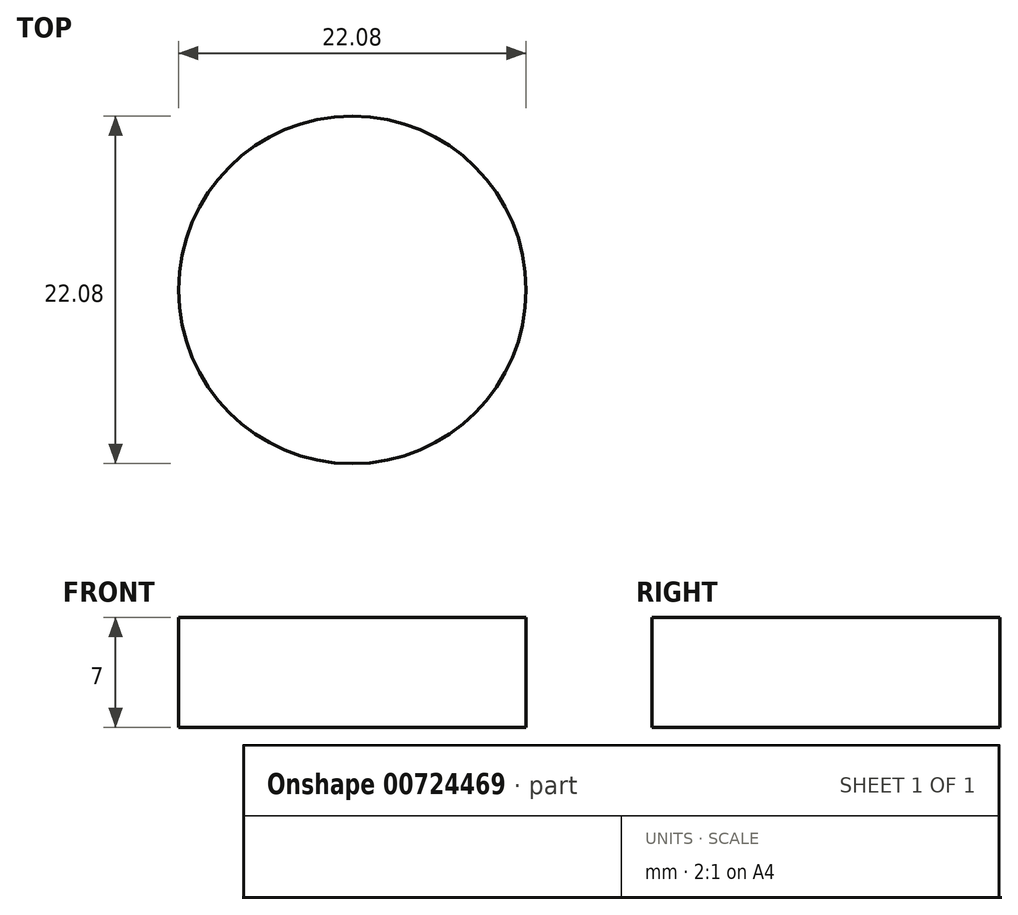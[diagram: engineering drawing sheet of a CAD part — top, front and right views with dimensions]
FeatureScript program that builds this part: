
annotation { "Feature Type Name" : "Feature", "Feature Type Description" : "" }
export const myFeature = defineFeature(function(context is Context, id is Id, definition is map)
    precondition{}
    {
        {
            var Q0;
            Q0=qCreatedBy(makeId("Top.planeOp"),FACE);
            var sketch = newSketch(context, id + "F0", { "sketchPlane" : qUnion([Q0])});
            skCircle(sketch, "E0", {"center": v(0, 0) * mm, "radius": 11.04 * mm});
            skSolve(sketch);
        }
        {
            var Q0;
            Q0 = qSketchRegion(id + "F0", true);
            extrude(context, id + "F1", {"entities" : qUnion([Q0]), "depth" : 7 * mm, "offsetDistance" : 25.4 * mm});
        }
    });
